# Revit family: TYBIA LED 38W-NW
name_source: partatom
category: Lighting Fixtures
revit_build: Autodesk Revit Architecture 2015 (Build: 20140322_1515(x64)
units: mm (PartAtom-declared; Revit-internal decimal feet)

## types (1)
- KANLUX TYBIA LED 38W-NW 24640 LED 4000K 110° 3500lm aluminium
    Apparent Load = 38 VA
    Color Filter = 16777215
    Default Elevation = 0 mm  [stored 0 ft]
    Dimming Lamp Color Temperature Shift = <None>
    Długość = 410 mm
    Emit Shape Visible in Rendering = Yes
    Emit from Rectangle Length = 370 mm  [stored 1.21391 ft]
    Emit from Rectangle Width = 370 mm  [stored 1.21391 ft]
    IP = IP20
    Klasyfikacja obciążenia = Oświetlenie
    Kod = 24640
    Kąt rozsyłu = 110°
    Lamp = LED
    Manufacturer = KANLUX
    Materiał klosz = KANLUX - klosz - tworzywo sztuczne (PMMA)
    Materiał obudowa = KANLUX - obudowa - aluminium
    Moc oprawy = 38 W
    Model = TYBIA LED 38W-NW
    Photometric Web File = TYBIA LED 38W-NW.ies
    Szerokość = 410 mm
    Tilt Angle = 90.00°
    URL = www.kanlux.pl
    Wattage Comments = 38
    Współczynnik mocy = 1
    Wysokość = 65 mm

note: [stored X ft] marks values corroborated as IEEE doubles in the binary element streams (Revit-internal decimal feet)
